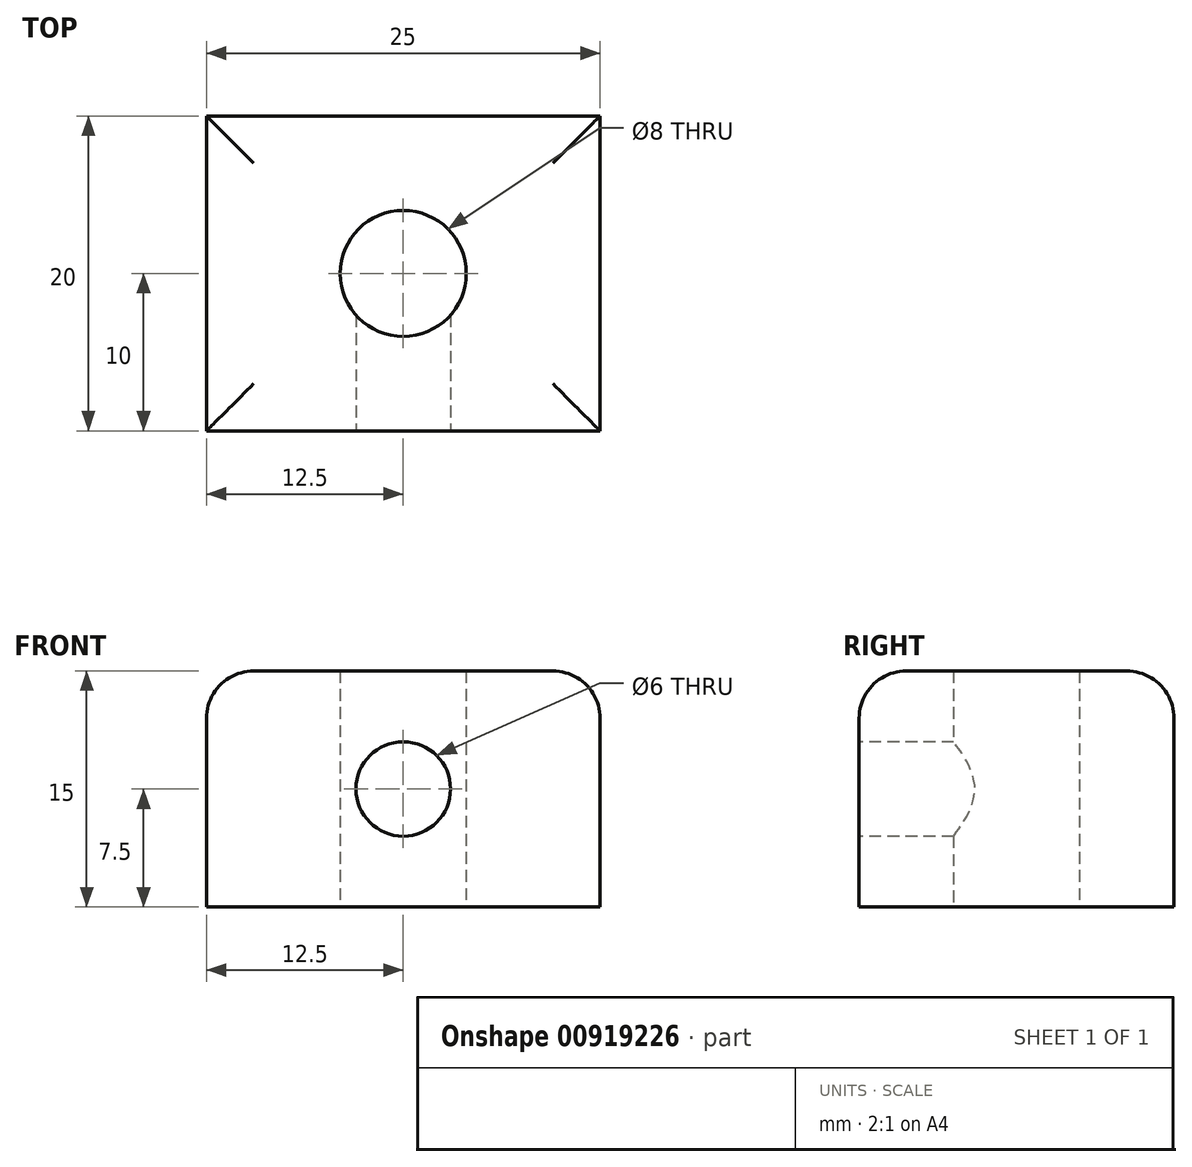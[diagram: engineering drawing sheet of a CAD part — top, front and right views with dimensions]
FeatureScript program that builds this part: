
annotation { "Feature Type Name" : "Feature", "Feature Type Description" : "" }
export const myFeature = defineFeature(function(context is Context, id is Id, definition is map)
    precondition{}
    {
        {
            var Q0;
            Q0=qCreatedBy(makeId("Top.planeOp"),FACE);
            var sketch = newSketch(context, id + "F0", { "sketchPlane" : qUnion([Q0])});
            skLineSegment(sketch, "E0.bottom", {"start": v(0, 0) * mm, "end": v(25, 0) * mm});
            skLineSegment(sketch, "E0.top", {"start": v(0, -20) * mm, "end": v(25, -20) * mm});
            skLineSegment(sketch, "E0.left", {"start": v(0, 0) * mm, "end": v(0, -20) * mm});
            skLineSegment(sketch, "E0.right", {"start": v(25, 0) * mm, "end": v(25, -20) * mm});
            skLineSegment(sketch, "E1", {"start": v(0, -10) * mm, "end": v(25, -10) * mm, "construction": true});
            skCircle(sketch, "E2", {"center": v(12.5, -10) * mm, "radius": 4 * mm});
            skSolve(sketch);
        }
        {
            var Q0;
            Q0=makeQuery(id+"F0.imprint","IMPRINT",FACE,{"disambiguationData":[TD([[makeQuery(id+"F0.imprint","IMPRINT",EDGE,{"derivedFrom":sQuery(id+"F0.wireOp",EDGE,"E0.bottom")}),-1.0]])]});
            extrude(context, id + "F1", {"entities" : qUnion([Q0]), "depth" : 15 * mm, "offsetDistance" : 25.4 * mm});
        }
        {
            var Q0;
            Q0=makeQuery(id+"F1.opExtrude","SWEPT_FACE",FACE,{"disambiguationData":[OSD([sQuery(id+"F0.wireOp",EDGE,"E0.top")])]});
            var sketch = newSketch(context, id + "F2", { "sketchPlane" : qUnion([Q0])});
            skLineSegment(sketch, "E3", {"start": v(0, 7.5) * mm, "end": v(25, 7.5) * mm, "construction": true});
            skCircle(sketch, "E4", {"center": v(12.5, 7.5) * mm, "radius": 3 * mm});
            skSolve(sketch);
        }
        {
            var Q0;
            Q0=makeQuery(id+"F2.imprint","IMPRINT",FACE,{"disambiguationData":[TD([[makeQuery(id+"F2.imprint","IMPRINT",EDGE,{"derivedFrom":sQuery(id+"F2.wireOp",EDGE,"E4")}),1.0]])]});
            extrude(context, id + "F3", {"entities" : qUnion([Q0]), "operationType" : NewBodyOperationType.REMOVE, "oppositeDirection" : true, "depth" : 10 * mm, "offsetDistance" : 25.4 * mm});
        }
        {
            var Q0;
            Q0=makeQuery(id+"F1.opExtrude","CAP_EDGE",EDGE,{"disambiguationData":[OSD([sQuery(id+"F0.wireOp",EDGE,"E0.left")])],"isStart":false});
            var Q1;
            Q1=makeQuery(id+"F1.opExtrude","CAP_EDGE",EDGE,{"disambiguationData":[OSD([sQuery(id+"F0.wireOp",EDGE,"E0.bottom")])],"isStart":false});
            var Q2;
            Q2=makeQuery(id+"F1.opExtrude","CAP_EDGE",EDGE,{"disambiguationData":[OSD([sQuery(id+"F0.wireOp",EDGE,"E0.right")])],"isStart":false});
            var Q3;
            Q3=makeQuery(id+"F1.opExtrude","CAP_EDGE",EDGE,{"disambiguationData":[OSD([sQuery(id+"F0.wireOp",EDGE,"E0.top")])],"isStart":false});
            fillet(context, id + "F4", {"entities" : qUnion([Q0, Q1, Q2, Q3]), "radius" : 3 * mm, "tangentPropagation" : true, "allowEdgeOverflow" : false});
        }
    });
